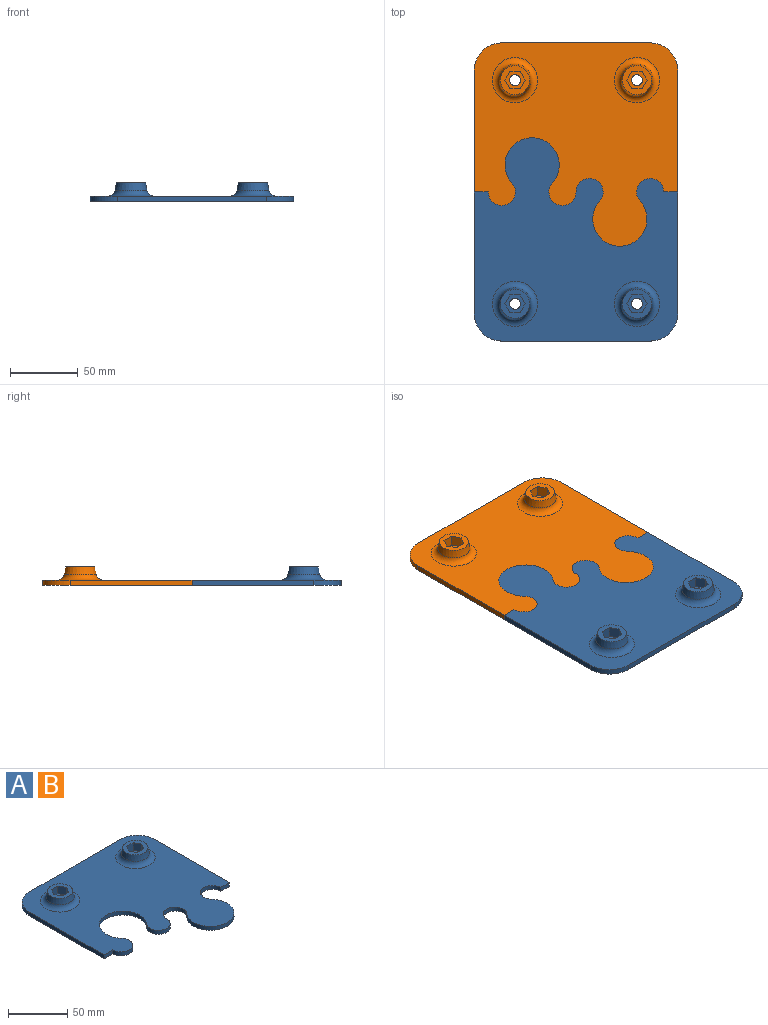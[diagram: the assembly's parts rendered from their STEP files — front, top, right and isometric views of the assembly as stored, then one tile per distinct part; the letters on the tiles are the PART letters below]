
ASSEMBLY  parts=2 mates=1
PART A: 37 faces, bbox 150x150x14 mm
  f0: plane 90x4mm, normal (1,0,0), area 360mm2, adj f2,f4,f9,f36
  f1: plane 90x4mm, normal (-1,0,0), area 360mm2, adj f2,f4,f10,f29
  f2: plane 150x150mm, normal (0,0,-1), area 16227.8mm2, adj f0,f1,f3,f9,f10,f27,f28,f29
  f3: plane 110x4mm, normal (0,1,0), area 440mm2, adj f2,f4,f9,f10
  f4: plane 150x150mm, normal (0,0,1), area 14576.9mm2, adj f0,f1,f3,f9,f10,f11,f12,f29
  f5: cone r=12.5mm half-angle=10deg, axis (0,0,-1), area 421.4mm2, adj f6,f11
  f6: plane 21.47x21.47mm, normal (0,0,1), area 215.8mm2, adj f5,f20,f21,f22,f23,f24,f25
  f7: cone r=12.5mm half-angle=10deg, axis (0,0,-1), area 421.4mm2, adj f8,f12
  f8: plane 21.47x21.47mm, normal (0,0,1), area 215.8mm2, adj f7,f13,f14,f15,f16,f17,f18
  f9: cylinder r=20mm len=20mm, axis (0,0,1), area 125.7mm2, adj f0,f2,f3,f4
  f10: cylinder r=20mm len=20mm, axis (0,0,-1), area 125.7mm2, adj f1,f2,f3,f4
  f11: torus R=16.7mm, axis (0,0,1), area 602.5mm2, adj f4,f5
  f12: torus R=16.7mm, axis (0,0,1), area 602.5mm2, adj f4,f7
  f13: plane 8x6.5mm, normal (0.87,0.5,0), area 60mm2, adj f8,f14,f18,f19
  f14: plane 8x7.51mm, normal (0,1,0), area 60mm2, adj f8,f13,f15,f19
  f15: plane 8x6.5mm, normal (-0.87,0.5,0), area 60mm2, adj f8,f14,f16,f19
  f16: plane 8x6.5mm, normal (-0.87,-0.5,0), area 60mm2, adj f8,f15,f17,f19
  f17: plane 8x7.51mm, normal (0,-1,0), area 60mm2, adj f8,f16,f18,f19
  f18: plane 8x6.5mm, normal (0.87,-0.5,0), area 60mm2, adj f8,f13,f17,f19
  f19: plane 15.01x13mm, normal (0,0,1), area 96.1mm2, adj f13,f14,f15,f16,f17,f18,f28
  f20: plane 8x6.5mm, normal (0.87,0.5,0), area 60mm2, adj f6,f21,f25,f26
  f21: plane 8x7.51mm, normal (0,1,0), area 60mm2, adj f6,f20,f22,f26
  f22: plane 8x6.5mm, normal (-0.87,0.5,0), area 60mm2, adj f6,f21,f23,f26
  f23: plane 8x6.5mm, normal (-0.87,-0.5,0), area 60mm2, adj f6,f22,f24,f26
  f24: plane 8x7.51mm, normal (0,-1,0), area 60mm2, adj f6,f23,f25,f26
  f25: plane 8x6.5mm, normal (0.87,-0.5,0), area 60mm2, adj f6,f20,f24,f26
  f26: plane 15.01x13mm, normal (0,0,1), area 96.1mm2, adj f20,f21,f22,f23,f24,f25,f27
  f27: cylinder r=4mm len=8mm, axis (0,0,1), area 150.8mm2, adj f2,f26
  f28: cylinder r=4mm len=8mm, axis (0,0,1), area 150.8mm2, adj f2,f19
  f29: plane 10.28x4mm, normal (0,-1,0), area 41.1mm2, adj f1,f2,f4,f30
  f30: cylinder r=10mm len=20mm, axis (0,0,-1), area 154.9mm2, adj f2,f4,f29,f31
  f31: cylinder r=20mm len=40mm, axis (0,0,-1), area 368.1mm2, adj f2,f4,f30,f32
  f32: cylinder r=10mm len=20mm, axis (0,0,-1), area 154.9mm2, adj f2,f4,f31,f33
  f33: cylinder r=10mm len=20mm, axis (0,0,-1), area 154.9mm2, adj f2,f4,f32,f34
  f34: cylinder r=20mm len=40mm, axis (0,0,-1), area 368.1mm2, adj f2,f4,f33,f35
  f35: cylinder r=10mm len=20mm, axis (0,0,-1), area 154.9mm2, adj f2,f4,f34,f36
  f36: plane 10.28x4mm, normal (0,-1,0), area 41.1mm2, adj f0,f2,f4,f35
PART B: same geometry as A
PLACE A rot(axis=(0,0,1),180deg) t=(12.09,28.45,11.7)mm
PLACE B t=(12.09,28.45,11.7)mm
MATE fastened A.f2 <-> B.f2  axis (0,0,1) through (-52.63,28.45,11.7)mm
